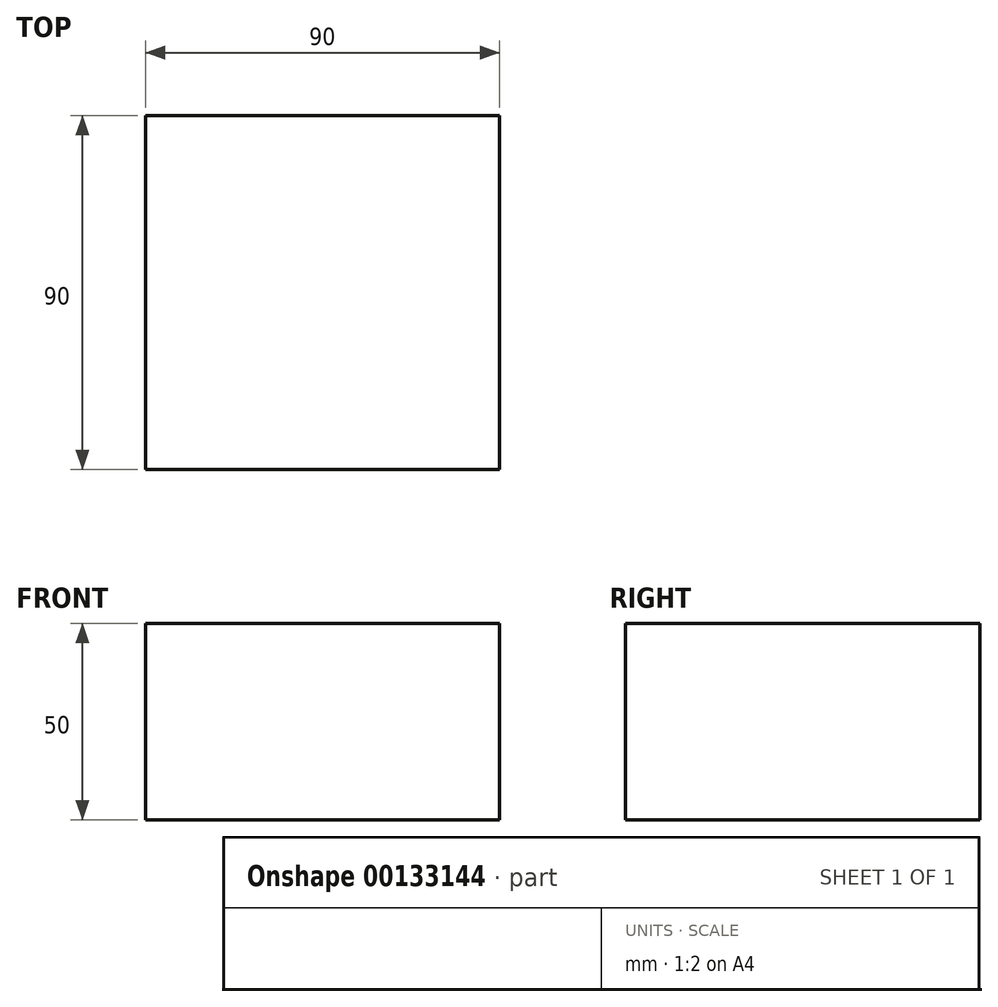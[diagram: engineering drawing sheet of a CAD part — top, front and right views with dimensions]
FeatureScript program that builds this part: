
annotation { "Feature Type Name" : "Feature", "Feature Type Description" : "" }
export const myFeature = defineFeature(function(context is Context, id is Id, definition is map)
    precondition{}
    {
        {
            var Q0;
            Q0=qCreatedBy(makeId("Top.planeOp"),FACE);
            var sketch = newSketch(context, id + "F0", { "sketchPlane" : qUnion([Q0])});
            skLineSegment(sketch, "E0.bottom", {"start": v(48.1, -11.94) * mm, "end": v(-41.9, -11.94) * mm});
            skLineSegment(sketch, "E0.top", {"start": v(48.1, 78.06) * mm, "end": v(-41.9, 78.06) * mm});
            skLineSegment(sketch, "E0.left", {"start": v(48.1, -11.94) * mm, "end": v(48.1, 78.06) * mm});
            skLineSegment(sketch, "E0.right", {"start": v(-41.9, -11.94) * mm, "end": v(-41.9, 78.06) * mm});
            skSolve(sketch);
        }
        {
            var Q0;
            Q0=qSketchRegion(id+"F0",true);
            extrude(context, id + "F1", {"entities" : qUnion([Q0]), "depth" : 50 * mm});
        }
    });
